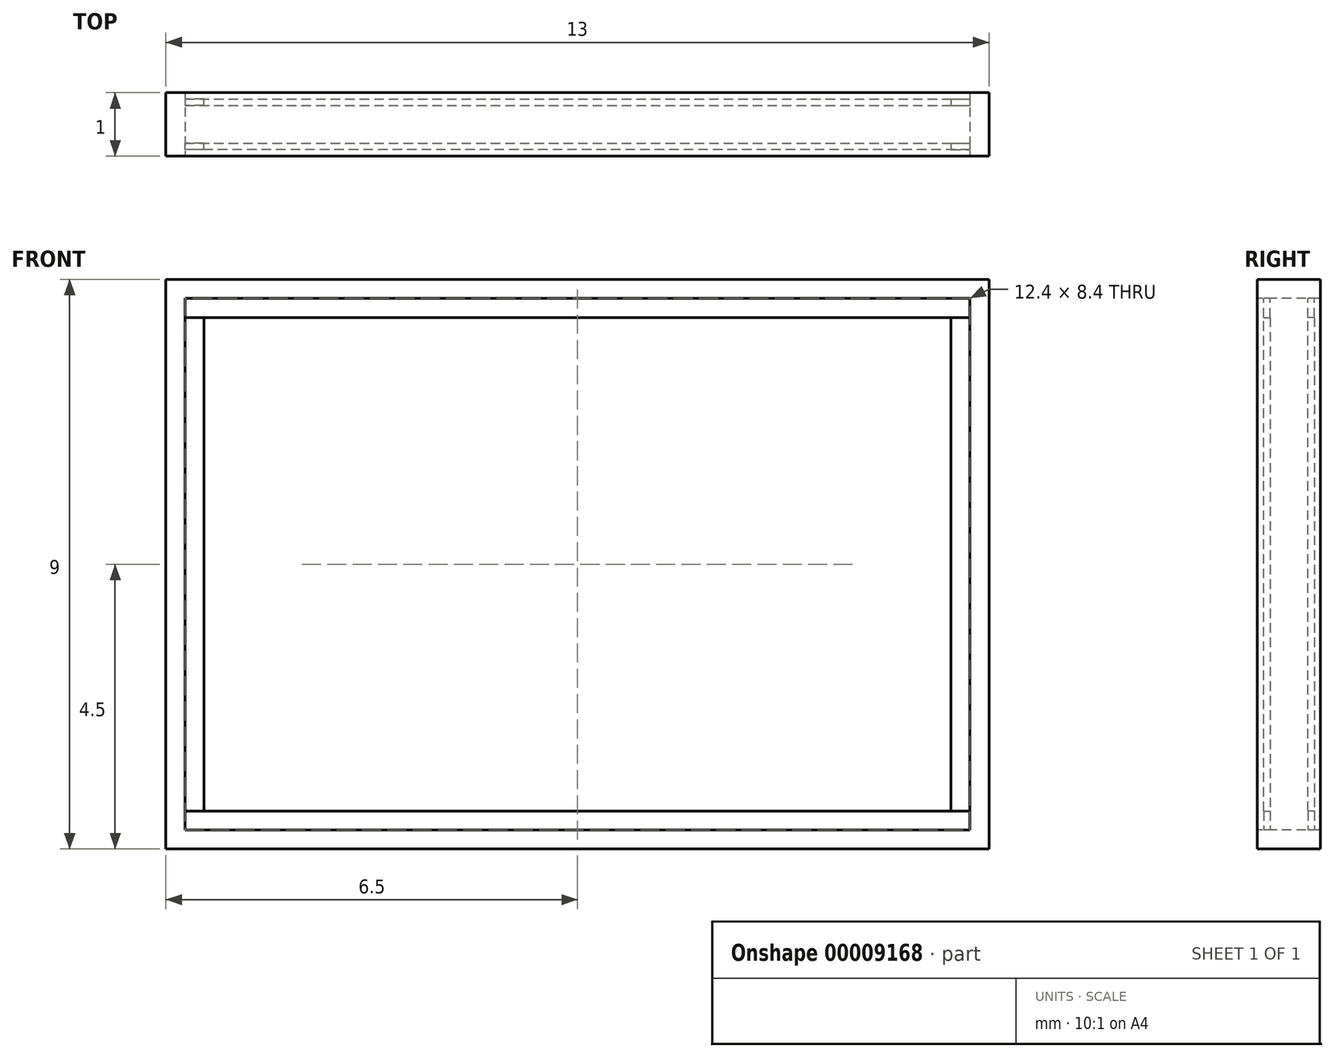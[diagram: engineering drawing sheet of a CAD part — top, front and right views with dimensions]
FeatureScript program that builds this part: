
annotation { "Feature Type Name" : "Feature", "Feature Type Description" : "" }
export const myFeature = defineFeature(function(context is Context, id is Id, definition is map)
    precondition{}
    {
        {
            var Q0;
            Q0=qCreatedBy(makeId("Top.planeOp"),FACE);
            var sketch = newSketch(context, id + "F0", { "sketchPlane" : qUnion([Q0])});
            skLineSegment(sketch, "E0.rect.bottom", {"start": v(6.5, 0.5) * mm, "end": v(-6.5, 0.5) * mm});
            skLineSegment(sketch, "E0.rect.top", {"start": v(6.5, -0.5) * mm, "end": v(-6.5, -0.5) * mm});
            skLineSegment(sketch, "E0.rect.left", {"start": v(6.5, 0.5) * mm, "end": v(6.5, -0.5) * mm});
            skLineSegment(sketch, "E0.rect.right", {"start": v(-6.5, 0.5) * mm, "end": v(-6.5, -0.5) * mm});
            skPoint(sketch, "E0.rect.middle", {"position": v(0, 0) * mm});
            skSolve(sketch);
        }
        {
            var Q0;
            Q0=makeQuery(id+"F0.imprint","IMPRINT",FACE,{"disambiguationData":[TD([[makeQuery(id+"F0.imprint","IMPRINT",EDGE,{"derivedFrom":sQuery(id+"F0.wireOp",EDGE,"E0.rect.bottom")}),1.0]])]});
            extrude(context, id + "F1", {"entities" : qUnion([Q0]), "depth" : 9 * mm});
        }
        {
            var Q0;
            Q0=makeQuery(id+"F1.opExtrude","SWEPT_FACE",FACE,{"disambiguationData":[OSD([sQuery(id+"F0.wireOp",EDGE,"E0.rect.top")])]});
            var sketch = newSketch(context, id + "F2", { "sketchPlane" : qUnion([Q0])});
            skLineSegment(sketch, "E1.rect.bottom", {"start": v(6.2, 8.7) * mm, "end": v(-6.2, 8.7) * mm});
            skLineSegment(sketch, "E1.rect.top", {"start": v(6.2, 0.3) * mm, "end": v(-6.2, 0.3) * mm});
            skLineSegment(sketch, "E1.rect.left", {"start": v(6.2, 8.7) * mm, "end": v(6.2, 0.3) * mm});
            skLineSegment(sketch, "E1.rect.right", {"start": v(-6.2, 8.7) * mm, "end": v(-6.2, 0.3) * mm});
            skPoint(sketch, "E1.rect.middle", {"position": v(0, 4.5) * mm});
            skSolve(sketch);
        }
        {
            var Q0;
            Q0 = qSketchRegion(id + "F2", true);
            extrude(context, id + "F3", {"entities" : qUnion([Q0]), "operationType" : NewBodyOperationType.REMOVE, "oppositeDirection" : true, "depth" : 25 * mm});
        }
        {
            var Q0;
            Q0=makeQuery(id+"F3.boolean.opBoolean","COPY",FACE,{"derivedFrom":makeQuery(id+"F3.opExtrude","SWEPT_FACE",FACE,{"disambiguationData":[OSD([sQuery(id+"F2.wireOp",EDGE,"E1.rect.top")])]})});
            var sketch = newSketch(context, id + "F4", { "sketchPlane" : qUnion([Q0])});
            skLineSegment(sketch, "E2.bottom", {"start": v(-6.2, -0.3) * mm, "end": v(6.2, -0.3) * mm});
            skLineSegment(sketch, "E2.top", {"start": v(-6.2, 0.3) * mm, "end": v(6.2, 0.3) * mm});
            skLineSegment(sketch, "E2.left", {"start": v(-6.2, -0.3) * mm, "end": v(-6.2, 0.3) * mm});
            skLineSegment(sketch, "E2.right", {"start": v(6.2, -0.3) * mm, "end": v(6.2, 0.3) * mm});
            skLineSegment(sketch, "E3", {"start": v(-6.2, -0.4) * mm, "end": v(6.2, -0.4) * mm});
            skLineSegment(sketch, "E4", {"start": v(-6.2, 0.4) * mm, "end": v(6.2, 0.4) * mm});
            skSolve(sketch);
        }
        {
            var Q0;
            {var subQ3=sQuery(id+"F4.wireOp",EDGE,"E2.top");Q0=makeQuery(id+"F4.imprint","IMPRINT",FACE,{"disambiguationData":[TD([[makeQuery(id+"F4.imprint","IMPRINT",EDGE,{"derivedFrom":subQ3}),1.0]])]});}
            var Q1;
            {var subQ3=sQuery(id+"F4.wireOp",EDGE,"E2.bottom");Q1=makeQuery(id+"F4.imprint","IMPRINT",FACE,{"disambiguationData":[TD([[makeQuery(id+"F4.imprint","IMPRINT",EDGE,{"derivedFrom":subQ3}),-1.0]])]});}
            extrude(context, id + "F5", {"entities" : qUnion([Q0, Q1]), "depth" : 0.3 * mm});
        }
        {
            var Q0;
            Q0=makeQuery(id+"F3.boolean.opBoolean","COPY",FACE,{"derivedFrom":makeQuery(id+"F3.opExtrude","SWEPT_FACE",FACE,{"disambiguationData":[OSD([sQuery(id+"F2.wireOp",EDGE,"E1.rect.bottom")])]})});
            var sketch = newSketch(context, id + "F6", { "sketchPlane" : qUnion([Q0])});
            skLineSegment(sketch, "E5.bottom", {"start": v(-6.2, 0.3) * mm, "end": v(6.2, 0.3) * mm});
            skLineSegment(sketch, "E5.top", {"start": v(-6.2, -0.3) * mm, "end": v(6.2, -0.3) * mm});
            skLineSegment(sketch, "E5.left", {"start": v(-6.2, 0.3) * mm, "end": v(-6.2, -0.3) * mm});
            skLineSegment(sketch, "E5.right", {"start": v(6.2, 0.3) * mm, "end": v(6.2, -0.3) * mm});
            skLineSegment(sketch, "E6", {"start": v(6.2, 0.4) * mm, "end": v(-6.2, 0.4) * mm});
            skLineSegment(sketch, "E7", {"start": v(-6.2, -0.4) * mm, "end": v(6.2, -0.4) * mm});
            skSolve(sketch);
        }
        {
            var Q0;
            {var subQ3=sQuery(id+"F6.wireOp",EDGE,"E5.top");Q0=makeQuery(id+"F6.imprint","IMPRINT",FACE,{"disambiguationData":[TD([[makeQuery(id+"F6.imprint","IMPRINT",EDGE,{"derivedFrom":subQ3}),-1.0]])]});}
            var Q1;
            {var subQ3=sQuery(id+"F6.wireOp",EDGE,"E5.bottom");Q1=makeQuery(id+"F6.imprint","IMPRINT",FACE,{"disambiguationData":[TD([[makeQuery(id+"F6.imprint","IMPRINT",EDGE,{"derivedFrom":subQ3}),1.0]])]});}
            extrude(context, id + "F7", {"entities" : qUnion([Q0, Q1]), "depth" : 0.3 * mm});
        }
        {
            var Q0;
            Q0=makeQuery(id+"F3.boolean.opBoolean","COPY",FACE,{"derivedFrom":makeQuery(id+"F3.opExtrude","SWEPT_FACE",FACE,{"disambiguationData":[OSD([sQuery(id+"F2.wireOp",EDGE,"E1.rect.right")])]})});
            var sketch = newSketch(context, id + "F8", { "sketchPlane" : qUnion([Q0])});
            skLineSegment(sketch, "E8", {"start": v(-0.4, 0.6) * mm, "end": v(-0.4, 8.4) * mm});
            skLineSegment(sketch, "E9", {"start": v(-0.3, 8.4) * mm, "end": v(-0.3, 0.6) * mm});
            skLineSegment(sketch, "E10", {"start": v(0.3, 0.6) * mm, "end": v(0.3, 8.4) * mm});
            skLineSegment(sketch, "E11", {"start": v(0.4, 8.4) * mm, "end": v(0.4, 0.6) * mm});
            skLineSegment(sketch, "E12", {"start": v(-0.4, 8.4) * mm, "end": v(-0.3, 8.4) * mm});
            skLineSegment(sketch, "E13", {"start": v(0.3, 8.4) * mm, "end": v(0.4, 8.4) * mm});
            skLineSegment(sketch, "E14", {"start": v(-0.4, 0.6) * mm, "end": v(-0.3, 0.6) * mm});
            skLineSegment(sketch, "E15", {"start": v(0.3, 0.6) * mm, "end": v(0.4, 0.6) * mm});
            skSolve(sketch);
        }
        {
            var Q0;
            Q0=makeQuery(id+"F3.boolean.opBoolean","COPY",FACE,{"derivedFrom":makeQuery(id+"F3.opExtrude","SWEPT_FACE",FACE,{"disambiguationData":[OSD([sQuery(id+"F2.wireOp",EDGE,"E1.rect.left")])]})});
            var sketch = newSketch(context, id + "F9", { "sketchPlane" : qUnion([Q0])});
            skLineSegment(sketch, "E16", {"start": v(0.4, 0.6) * mm, "end": v(0.4, 8.4) * mm});
            skLineSegment(sketch, "E17", {"start": v(0.3, 8.4) * mm, "end": v(0.3, 0.6) * mm});
            skLineSegment(sketch, "E18", {"start": v(-0.3, 0.6) * mm, "end": v(-0.3, 8.4) * mm});
            skLineSegment(sketch, "E19", {"start": v(-0.4, 8.4) * mm, "end": v(-0.4, 0.6) * mm});
            skLineSegment(sketch, "E20", {"start": v(0.3, 0.6) * mm, "end": v(0.4, 0.6) * mm});
            skLineSegment(sketch, "E21", {"start": v(-0.4, 0.6) * mm, "end": v(-0.3, 0.6) * mm});
            skLineSegment(sketch, "E22", {"start": v(0.3, 8.4) * mm, "end": v(0.4, 8.4) * mm});
            skLineSegment(sketch, "E23", {"start": v(-0.3, 8.4) * mm, "end": v(-0.4, 8.4) * mm});
            skSolve(sketch);
        }
        {
            var Q0;
            Q0 = qSketchRegion(id + "F8", true);
            extrude(context, id + "F10", {"entities" : qUnion([Q0]), "depth" : 0.3 * mm});
        }
        {
            var Q0;
            Q0 = qSketchRegion(id + "F9", true);
            extrude(context, id + "F11", {"entities" : qUnion([Q0]), "depth" : 0.3 * mm});
        }
    });
